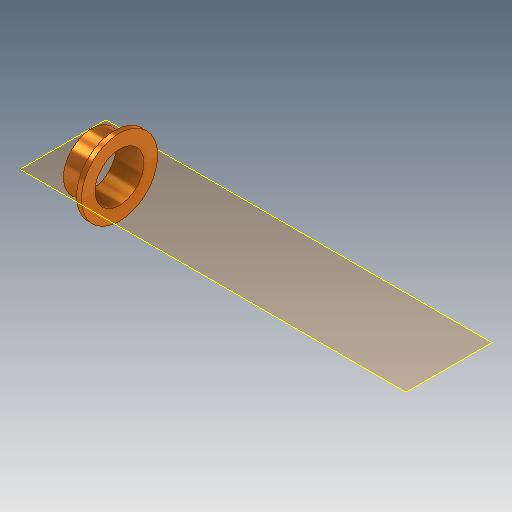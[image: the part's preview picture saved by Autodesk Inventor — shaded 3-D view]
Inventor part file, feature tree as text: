
AUTODESK INVENTOR PART (.ipt)
format: ipt  version: 2025 (Build 290162000, 162)  size: 109,568 bytes
history: native  units: mm
features: other x8, reference x4, plane x1, revolve x1, sketch x1
ambient origin geometry x8: Origin, YZ Plane, XZ Plane, XY Plane, X Axis, Y Axis, Z Axis, Center Point
bodies: 实体1 (feature_tree)
feature tree (15):
  plane  "工作平面1"
  revolve  "旋转1"  [1 undecoded]
  sketch  "草图1"  dims[d0=4.0mm d1=10.0mm d2=5.0mm d3=90.0deg]
  reference  "参考1"
  reference  "参考2"
  reference  "参考3"
  reference  "参考4"
  other  "齿轮箱.iam"
  other  "低速轴:1"
  other  "轴承:1"
  other  "滚动轴承 GB/T 276-1994 60000 和 160000 型 6010:1"
  other  "低速齿轮:1"
  other  "正齿轮:1"
  other  "正齿轮2:1"
  other  "轴:1"
note: 1 required parameter value undecoded (feature->parameter linkage not recoverable at this tier; creation-order binding heuristic only, values carry confidence <= 0.55)
